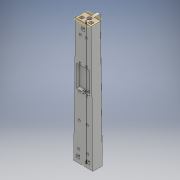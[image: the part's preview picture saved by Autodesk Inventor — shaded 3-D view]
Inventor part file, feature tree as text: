
AUTODESK INVENTOR PART (.ipt)
format: ipt  version: 2017 (Build 210142000, 142)  size: 480,768 bytes
history: native  units: mm
features: sketch x37, extrude x29, chamfer x10, loft x2, plane x1, other x1, hole x1
ambient origin geometry x8: Origin, YZ Plane, XZ Plane, XY Plane, X Axis, Y Axis, Z Axis, Center Point
bodies: Solid1 (feature_tree)
feature tree (81):
  sketch  "Sketch1"  dims[d0=31.0mm d1=15.0mm]
  sketch  "Sketch2"  dims[d2=12.5mm d3=11.0mm]
  sketch  "Sketch3"  dims[d4=10.0mm d5=200.0mm]
  plane  "Work Plane1"
  sketch  "Sketch4"  dims[d6=25.0mm d7=15.0mm]
  sketch  "Sketch5"  dims[d8=12.5mm d9=5.0mm]
  loft  "Loft1"
  loft  "Loft2"
  other  "Work Point1"
  sketch  "Sketch15"  dims[d10=10.0mm d11=0.0mm d12=90.0deg]
  sketch  "Sketch16"  dims[d13=0.0mm d14=90.0deg d15=0.0mm d16=90.0deg]
  sketch  "Sketch18"  dims[d79=0.0mm d80=2.0mm]
  sketch  "Sketch19"  dims[d81=0.0mm d82=1.2mm]
  sketch  "Sketch20"  dims[d83=1.2mm d84=6.6mm d85=0.0mm]
  extrude  "Extrusion17"  Depth=200.0mm
  extrude  "Extrusion18"  Depth=15.0mm
  extrude  "Extrusion19"  Depth=5.0mm
  extrude  "Extrusion20"  TaperAngle=0.0deg  [1 undecoded]
  extrude  "Extrusion21"  TaperAngle=0.0deg  [1 undecoded]
  extrude  "Extrusion22"  Depth=2.0mm
  extrude  "Extrusion23"  Depth=2.0mm
  extrude  "Extrusion24"  Depth=1.2mm
  extrude  "Extrusion25"  Depth=6.6mm TaperAngle=0.0deg
  extrude  "Extrusion26"  Depth=2.8mm
  extrude  "Extrusion27"  Depth=2.0mm
  extrude  "Extrusion28"  TaperAngle=0.0deg  [1 undecoded]
  extrude  "Extrusion29"  TaperAngle=0.0deg  [1 undecoded]
  extrude  "Extrusion30"  Depth=1.2mm
  extrude  "Extrusion31"  Depth=2.8mm
  extrude  "Extrusion32"  Depth=8.0mm TaperAngle=0.0deg
  extrude  "Extrusion33"  Depth=1.2mm
  extrude  "Extrusion34"  Depth=2.8mm
  extrude  "Extrusion35"  Depth=8.0mm TaperAngle=0.0deg
  extrude  "Extrusion36"  Depth=1.2mm
  chamfer  "Chamfer1"  Distance=6.6mm
  chamfer  "Chamfer2"  Distance=8.0mm
  chamfer  "Chamfer3"  Distance=6.6mm
  chamfer  "Chamfer4"  Distance=8.0mm
  chamfer  "Chamfer5"  Distance=6.6mm
  chamfer  "Chamfer6"  Distance=8.0mm
  chamfer  "Chamfer7"  Distance=1.2mm
  chamfer  "Chamfer8"  Distance=6.6mm
  chamfer  "Chamfer9"  Distance=2.8mm
  chamfer  "Chamfer10"  Distance=2.8mm
  hole  "Hole2"  [1 undecoded]
  sketch  "Sketch37"  dims[d123=2.8mm]
  sketch  "Sketch38"  dims[d124=2.8mm d125=8.0mm d126=0.0mm]
  sketch  "Sketch39"  dims[d127=2.0mm]
  extrude  "Extrusion37"  Depth=2.0mm
  extrude  "Extrusion38"  Depth=1.2mm
  extrude  "Extrusion47"  Depth=1.2mm
  extrude  "Extrusion48"  Depth=6.6mm TaperAngle=0.0deg
  extrude  "Extrusion49"  Depth=2.8mm
  sketch  "Sketch53"  dims[d133=2.8mm]
  sketch  "Sketch54"  dims[d134=2.8mm d135=8.0mm d136=0.0mm]
  extrude  "Extrusion50"  Depth=2.8mm
  extrude  "Extrusion51"  Depth=8.0mm TaperAngle=0.0deg
  sketch  "Sketch58"  dims[d138=180.0deg]
  sketch  "Sketch59"  dims[d139=1.2mm d140=1.2mm d141=6.6mm d142=0.0mm d143=2.8mm d144=2.8mm d145=8.0mm d146=0.0mm d147=2.0mm d148=1.2mm d149=1.2mm d150=6.6mm d151=0.0mm d152=2.8mm d153=2.8mm d154=8.0mm d155=0.0mm d156=2.0mm d157=180.0deg d158=1.2mm d159=1.2mm d160=6.6mm d161=0.0mm d162=2.8mm d163=2.8mm d164=8.0mm d165=0.0mm d166=2.0mm d167=180.0deg d168=1.2mm d169=1.2mm d170=6.6mm d171=0.0mm d172=2.8mm d173=2.8mm d174=8.0mm d175=0.0mm d176=0.8mm d177=2.0mm d178=45.0deg d179=0.8mm d180=2.0mm d181=45.0deg d182=0.8mm d183=2.0mm d184=45.0deg d185=0.8mm d186=2.0mm d187=45.0deg d188=0.8mm d189=2.0mm d190=45.0deg d191=0.71mm d192=2.0mm d193=45.0deg d194=0.7mm d195=2.0mm d196=45.0deg d197=0.8mm d198=2.0mm d199=45.0deg d200=0.7mm d201=2.0mm d202=45.0deg d203=0.7mm d204=2.0mm d205=45.0deg d206=15.0mm d207=6.4mm d208=6.0mm d209=4.0mm d210=2.0mm d211=90.0deg d212=8.0mm d213=20.594885mm d214=7.5mm d215=9.0mm d216=5.0mm d217=5.0mm d218=7.5mm d219=9.0mm d220=5.0mm d221=5.0mm d230=6.0mm d231=0.0mm d232=6.0mm d233=0.0mm d260=21.0mm d261=35.0mm d262=5.0mm d263=0.0mm d264=5.0mm d265=5.0mm d266=0.0mm d267=5.0mm d268=5.0mm d269=5.0mm d270=0.0mm d271=4.75mm d272=4.75mm d273=5.5mm d274=5.5mm d275=6.0mm d276=0.0mm d277=4.75mm d278=4.75mm d279=5.5mm d280=5.5mm d281=6.0mm d282=0.0mm d289=2.5mm d290=2.5mm d291=5.0mm d292=5.0mm d293=2.5mm d294=2.5mm d295=5.0mm d296=5.0mm d297=6.0mm d298=0.0mm d299=6.0mm d300=0.0mm]
  extrude  "Extrusion52"  Depth=2.0mm
  extrude  "Extrusion53"  TaperAngle=180.0deg  [1 undecoded]
  sketch  "Sketch17"  dims[d17=0.0mm d18=90.0deg d78=2.0mm]
  sketch  "Sketch21"  dims[d86=2.8mm d87=2.8mm]
  sketch  "Sketch22"  dims[d88=8.0mm d89=0.0mm d90=2.0mm]
  sketch  "Sketch23"  dims[d91=2.0mm d92=0.0mm]
  sketch  "Sketch24"  dims[d93=2.0mm d94=0.0mm]
  sketch  "Sketch26"  dims[d95=1.2mm d96=1.2mm]
  sketch  "Sketch27"  dims[d97=6.6mm d98=0.0mm d99=2.8mm]
  sketch  "Sketch28"  dims[d100=2.8mm d101=8.0mm d102=0.0mm]
  sketch  "Sketch29"  dims[d103=1.2mm d104=1.2mm]
  sketch  "Sketch30"  dims[d105=6.6mm d106=0.0mm d107=2.8mm]
  sketch  "Sketch31"  dims[d108=2.8mm d109=8.0mm d110=0.0mm]
  sketch  "Sketch32"  dims[d111=1.2mm d112=1.2mm d113=6.6mm d114=0.0mm]
  sketch  "Sketch33"  dims[d115=2.8mm]
  sketch  "Sketch34"  dims[d116=2.8mm d117=8.0mm d118=0.0mm]
  sketch  "Sketch35"  dims[d119=1.2mm]
  sketch  "Sketch36"  dims[d120=1.2mm d121=6.6mm d122=0.0mm]
  sketch  "Sketch49"  dims[d128=180.0deg]
  sketch  "Sketch50"  dims[d129=1.2mm]
  sketch  "Sketch51"  dims[d130=1.2mm d131=6.6mm d132=0.0mm]
  sketch  "Sketch55"  dims[d137=2.0mm]
note: 6 required parameter values undecoded (feature->parameter linkage not recoverable at this tier; creation-order binding heuristic only, values carry confidence <= 0.55)
